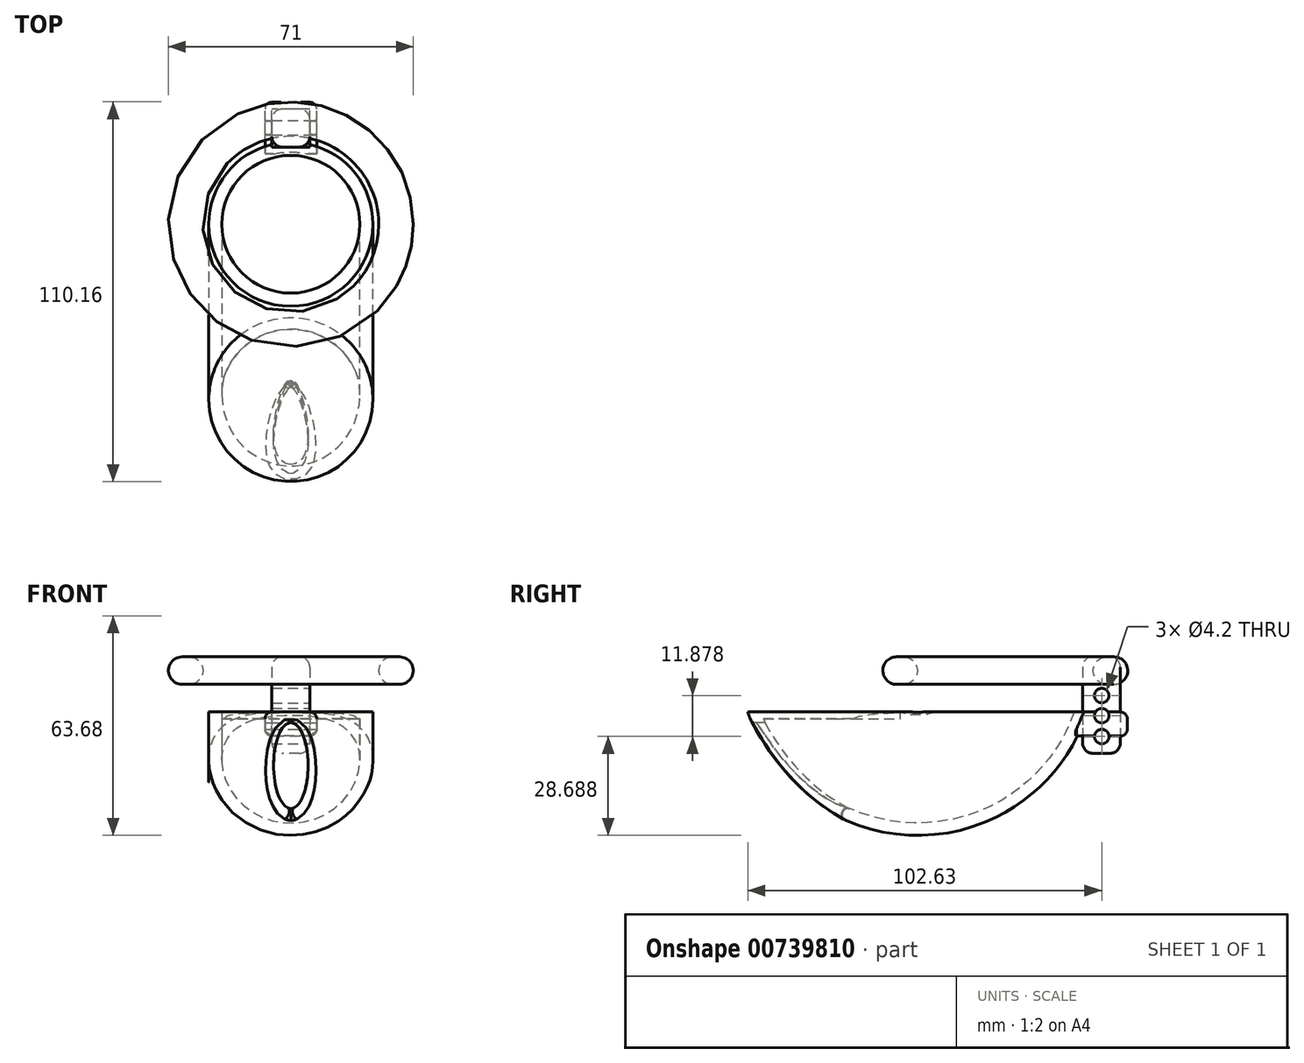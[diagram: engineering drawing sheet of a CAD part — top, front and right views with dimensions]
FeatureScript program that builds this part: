
annotation { "Feature Type Name" : "Feature", "Feature Type Description" : "" }
export const myFeature = defineFeature(function(context is Context, id is Id, definition is map)
    precondition{}
    {
        {
            var Q0;
            Q0=qCreatedBy(makeId("Front.planeOp"),FACE);
            cPlane(context, id + "F0", {"entities" : qUnion([Q0]), "cplaneType" : CPlaneType.OFFSET, "offset" : 25 * mm, "width" : 150 * mm, "height" : 150 * mm});
        }
        {
            var Q0;
            Q0=qCreatedBy(makeId("Top.planeOp"),FACE);
            var sketch = newSketch(context, id + "F1", { "sketchPlane" : qUnion([Q0])});
            skCircle(sketch, "E0", {"center": v(0, 0) * mm, "radius": 23.8 * mm});
            skCircle(sketch, "E1", {"center": v(0, 0) * mm, "radius": 20 * mm});
            skSolve(sketch);
        }
        {
            var Q0;
            Q0=qCreatedBy(makeId("Right.planeOp"),FACE);
            var sketch = newSketch(context, id + "F2", { "sketchPlane" : qUnion([Q0])});
            skArc(sketch, "E2", {"start": v(-55.13, 20.16) * mm, "mid": v(-35.74, -12.26) * mm, "end": v(0, 0) * mm});
            skSolve(sketch);
        }
        {
            var Q0;
            Q0=makeQuery(id+"F1.imprint","IMPRINT",FACE,{"disambiguationData":[TD([[makeQuery(id+"F1.imprint","IMPRINT",EDGE,{"derivedFrom":sQuery(id+"F1.wireOp",EDGE,"E0")}),1.0]])]});
            var Q1;
            Q1=sQuery(id+"F2.wireOp",EDGE,"E2");
            sweep(context, id + "F3", {"profiles" : qUnion([Q0]), "path" : qUnion([Q1])});
        }
        {
            var Q0;
            Q0=qCreatedBy(makeId("Right.planeOp"),FACE);
            var sketch = newSketch(context, id + "F4", { "sketchPlane" : qUnion([Q0])});
            skLineSegment(sketch, "E3.bottom", {"start": v(-24.7, 0) * mm, "end": v(-163.66, 0) * mm});
            skLineSegment(sketch, "E3.top", {"start": v(-24.7, 86.96) * mm, "end": v(-163.66, 86.96) * mm});
            skLineSegment(sketch, "E3.left", {"start": v(-24.7, 0) * mm, "end": v(-24.7, 86.96) * mm});
            skLineSegment(sketch, "E3.right", {"start": v(-163.66, 0) * mm, "end": v(-163.66, 86.96) * mm});
            skPoint(sketch, "E3.middle", {"position": v(-94.18, 43.48) * mm});
            skSolve(sketch);
        }
        {
            var Q0;
            Q0=qSketchRegion(id+"F4",true);
            extrude(context, id + "F5", {"entities" : qUnion([Q0]), "operationType" : NewBodyOperationType.REMOVE, "depth" : 25 * mm, "offsetDistance" : 25 * mm, "hasSecondDirection" : true, "secondDirectionOppositeDirection" : true, "secondDirectionDepth" : 25 * mm});
        }
        {
            var Q0;
            Q0=qCreatedBy(makeId("Top.planeOp"),FACE);
            var sketch = newSketch(context, id + "F6", { "sketchPlane" : qUnion([Q0])});
            skCircle(sketch, "E4", {"center": v(0, -50.93) * mm, "radius": 20.5 * mm});
            skSolve(sketch);
        }
        {
            var Q0;
            Q0=makeQuery(id+"F6.imprint","IMPRINT",FACE,{"disambiguationData":[TD([[makeQuery(id+"F6.imprint","IMPRINT",EDGE,{"derivedFrom":sQuery(id+"F6.wireOp",EDGE,"c734bf54-2df6-41e3-86b9-9994cdd1f29b")}),1.0]])]});
            var Q1;
            Q1=makeQuery(id+"F6.imprint","IMPRINT",FACE,{"disambiguationData":[TD([[makeQuery(id+"F6.imprint","IMPRINT",EDGE,{"derivedFrom":sQuery(id+"F6.wireOp",EDGE,"E4")}),1.0]])]});
            extrude(context, id + "F7", {"entities" : qUnion([Q0, Q1]), "operationType" : NewBodyOperationType.ADD, "oppositeDirection" : true, "depth" : 2 * mm, "offsetDistance" : 25 * mm});
        }
        {
            var Q0;
            Q0=qCreatedBy(id+"F0.planeOp",FACE);
            var sketch = newSketch(context, id + "F8", { "sketchPlane" : qUnion([Q0])});
            skEllipse(sketch, "E5", {"center": v(0, -15.52) * mm, "majorRadius": 12.5 * mm, "minorRadius": 5 * mm, "majorAxis": v(0, 1)});
            skSolve(sketch);
        }
        {
            var Q0;
            Q0=qSketchRegion(id+"F8",true);
            extrude(context, id + "F9", {"entities" : qUnion([Q0]), "operationType" : NewBodyOperationType.REMOVE, "depth" : 75 * mm, "offsetDistance" : 25 * mm, "hasSecondDirection" : true, "secondDirectionOppositeDirection" : false, "secondDirectionDepth" : 9.6 * mm});
        }
        {
            var Q0;
            Q0=makeQuery(id+"F9.boolean.opBoolean","INTERSECT",EDGE,{"derivedFrom":[makeQuery(id+"F3.opSweep","SWEPT_FACE",FACE,{"disambiguationData":[OSD([sQuery(id+"F1.wireOp",EDGE,"E0"),sQuery(id+"F2.wireOp",EDGE,"E2")])]}),makeQuery(id+"F9.opExtrude","SWEPT_FACE",FACE,{"disambiguationData":[OSD([sQuery(id+"F8.wireOp",EDGE,"E5")])]})]});
            fillet(context, id + "F10", {"entities" : qUnion([Q0]), "radius" : 1.8 * mm, "tangentPropagation" : true, "allowEdgeOverflow" : false});
        }
        {
            var Q0;
            Q0=qCreatedBy(makeId("Top.planeOp"),FACE);
            var sketch = newSketch(context, id + "F11", { "sketchPlane" : qUnion([Q0])});
            skLineSegment(sketch, "E6.bottom", {"start": v(7.5, 20.39) * mm, "end": v(-7.5, 20.39) * mm});
            skLineSegment(sketch, "E6.top", {"start": v(7.5, 35.39) * mm, "end": v(-7.5, 35.39) * mm});
            skLineSegment(sketch, "E6.left", {"start": v(7.5, 20.39) * mm, "end": v(7.5, 35.39) * mm});
            skLineSegment(sketch, "E6.right", {"start": v(-7.5, 20.39) * mm, "end": v(-7.5, 35.39) * mm});
            skPoint(sketch, "E6.middle", {"position": v(0, 27.89) * mm});
            skLineSegment(sketch, "E7.0", {"start": v(5.5, 33.39) * mm, "end": v(-5.5, 33.39) * mm});
            skLineSegment(sketch, "E7.1", {"start": v(5.5, 22.39) * mm, "end": v(5.5, 33.39) * mm});
            skLineSegment(sketch, "E7.2", {"start": v(5.5, 22.39) * mm, "end": v(-5.5, 22.39) * mm});
            skLineSegment(sketch, "E7.3", {"start": v(-5.5, 22.39) * mm, "end": v(-5.5, 33.39) * mm});
            skSolve(sketch);
        }
        {
            var Q0;
            Q0=makeQuery(id+"F11.imprint","IMPRINT",FACE,{"disambiguationData":[TD([[makeQuery(id+"F11.imprint","IMPRINT",EDGE,{"derivedFrom":sQuery(id+"F11.wireOp",EDGE,"E6.bottom")}),-1.0]])]});
            extrude(context, id + "F12", {"entities" : qUnion([Q0]), "operationType" : NewBodyOperationType.ADD, "oppositeDirection" : true, "depth" : 7 * mm, "offsetDistance" : 25 * mm});
        }
        {
            var Q0;
            Q0=makeQuery(id+"F11.imprint","IMPRINT",FACE,{"disambiguationData":[TD([[makeQuery(id+"F11.imprint","IMPRINT",EDGE,{"derivedFrom":sQuery(id+"F11.wireOp",EDGE,"E7.0")}),1.0]])]});
            extrude(context, id + "F13", {"entities" : qUnion([Q0]), "operationType" : NewBodyOperationType.REMOVE, "oppositeDirection" : true, "depth" : 5 * mm, "offsetDistance" : 25 * mm, "hasSecondDirection" : true, "secondDirectionOppositeDirection" : false, "secondDirectionDepth" : 5 * mm});
        }
        {
            var Q0;
            Q0=makeQuery(id+"F12.opExtrude","SWEPT_FACE",FACE,{"disambiguationData":[OSD([sQuery(id+"F11.wireOp",EDGE,"E6.top")])]});
            var Q1;
            Q1=makeQuery(id+"F12.opExtrude","CAP_EDGE",EDGE,{"disambiguationData":[OSD([sQuery(id+"F11.wireOp",EDGE,"E6.left")])],"isStart":false});
            var Q2;
            Q2=makeQuery(id+"F12.opExtrude","CAP_EDGE",EDGE,{"disambiguationData":[OSD([sQuery(id+"F11.wireOp",EDGE,"E6.left")])],"isStart":true});
            var Q3;
            Q3=makeQuery(id+"F12.opExtrude","CAP_EDGE",EDGE,{"disambiguationData":[OSD([sQuery(id+"F11.wireOp",EDGE,"E6.right")])],"isStart":true});
            var Q4;
            Q4=makeQuery(id+"F12.opExtrude","CAP_EDGE",EDGE,{"disambiguationData":[OSD([sQuery(id+"F11.wireOp",EDGE,"E6.right")])],"isStart":false});
            fillet(context, id + "F14", {"entities" : qUnion([Q0, Q1, Q2, Q3, Q4]), "radius" : 2 * mm, "tangentPropagation" : true, "allowEdgeOverflow" : false});
        }
        {
            var Q0;
            Q0=qCreatedBy(makeId("Top.planeOp"),FACE);
            var sketch = newSketch(context, id + "F15", { "sketchPlane" : qUnion([Q0])});
            skCircle(sketch, "E8", {"center": v(0, 0) * mm, "radius": 25.5 * mm});
            skCircle(sketch, "E9.0", {"center": v(0, 0) * mm, "radius": 35.5 * mm});
            skSolve(sketch);
        }
        {
            var Q0;
            Q0 = qSketchRegion(id + "F15", true);
            extrude(context, id + "F16", {"entities" : qUnion([Q0]), "depth" : 16 * mm, "offsetDistance" : 25 * mm, "hasSecondDirection" : true, "secondDirectionOppositeDirection" : false, "secondDirectionDepth" : 8 * mm});
        }
        {
            var Q0;
            Q0=makeQuery(id+"F16.opExtrude","SWEPT_FACE",FACE,{"disambiguationData":[OSD([sQuery(id+"F15.wireOp",EDGE,"E9.0")])]});
            var Q1;
            Q1=makeQuery(id+"F16.opExtrude","SWEPT_FACE",FACE,{"disambiguationData":[OSD([sQuery(id+"F15.wireOp",EDGE,"E8")])]});
            fillet(context, id + "F17", {"entities" : qUnion([Q0, Q1]), "radius" : 4 * mm, "tangentPropagation" : true, "allowEdgeOverflow" : false});
        }
        {
            var Q0;
            Q0=makeQuery(id+"F11.imprint","IMPRINT",FACE,{"disambiguationData":[TD([[makeQuery(id+"F11.imprint","IMPRINT",EDGE,{"derivedFrom":sQuery(id+"F11.wireOp",EDGE,"E7.0")}),1.0]])]});
            extrude(context, id + "F18", {"entities" : qUnion([Q0]), "depth" : 16 * mm, "offsetDistance" : 25 * mm, "hasSecondDirection" : true, "secondDirectionOppositeDirection" : true, "secondDirectionDepth" : 12 * mm});
        }
        {
            var Q0;
            Q0=makeQuery(id+"FuZBCL0iS8PPMPQ_3.boolean.opBoolean","COPY",FACE,{"derivedFrom":makeQuery(id+"FuZBCL0iS8PPMPQ_3.opThicken","CAP_FACE",FACE,{"disambiguationData":[OSD([sQuery(id+"F11.wireOp",EDGE,"E7.0")])],"isStart":false})});
            var Q1;
            Q1=makeQuery(id+"FuZBCL0iS8PPMPQ_3.boolean.opBoolean","COPY",FACE,{"derivedFrom":makeQuery(id+"FuZBCL0iS8PPMPQ_3.opThicken","CAP_FACE",FACE,{"disambiguationData":[OSD([sQuery(id+"F11.wireOp",EDGE,"E7.2")])],"isStart":false})});
            var Q2;
            Q2=makeQuery(id+"F18.opExtrude","SWEPT_EDGE",EDGE,{"disambiguationData":[OSD([sQuery(id+"F11.wireOp",EDGE,"E7.0"),sQuery(id+"F11.wireOp",EDGE,"E7.1")])]});
            var Q3;
            Q3=makeQuery(id+"F18.opExtrude","SWEPT_EDGE",EDGE,{"disambiguationData":[OSD([sQuery(id+"F11.wireOp",EDGE,"E7.1"),sQuery(id+"F11.wireOp",EDGE,"E7.2")])]});
            var Q4;
            Q4=makeQuery(id+"F18.opExtrude","SWEPT_EDGE",EDGE,{"disambiguationData":[OSD([sQuery(id+"F11.wireOp",EDGE,"E7.0"),sQuery(id+"F11.wireOp",EDGE,"E7.3")])]});
            var Q5;
            Q5=makeQuery(id+"F18.opExtrude","SWEPT_EDGE",EDGE,{"disambiguationData":[OSD([sQuery(id+"F11.wireOp",EDGE,"E7.2"),sQuery(id+"F11.wireOp",EDGE,"E7.3")])]});
            var Q6;
            Q6=makeQuery(id+"F18.opExtrude","CAP_FACE",FACE,{"disambiguationData":[OSD([sQuery(id+"F11.wireOp",EDGE,"E7.0"),sQuery(id+"F11.wireOp",EDGE,"E7.1"),sQuery(id+"F11.wireOp",EDGE,"E7.2"),sQuery(id+"F11.wireOp",EDGE,"E7.3")])],"isStart":true});
            var Q7;
            Q7=makeQuery(id+"F18.opExtrude","CAP_FACE",FACE,{"disambiguationData":[OSD([sQuery(id+"F11.wireOp",EDGE,"E7.0"),sQuery(id+"F11.wireOp",EDGE,"E7.1"),sQuery(id+"F11.wireOp",EDGE,"E7.2"),sQuery(id+"F11.wireOp",EDGE,"E7.3")])],"isStart":false});
            fillet(context, id + "F19", {"entities" : qUnion([Q0, Q1, Q2, Q3, Q4, Q5, Q6, Q7]), "radius" : 3 * mm, "tangentPropagation" : true, "allowEdgeOverflow" : false});
        }
        {
            var Q0;
            Q0=qCreatedBy(makeId("Right.planeOp"),FACE);
            var sketch = newSketch(context, id + "F20", { "sketchPlane" : qUnion([Q0])});
            skCircle(sketch, "E10", {"center": v(27.97, -7.13) * mm, "radius": 2.1 * mm});
            skPoint(sketch, "E10.centerSnap0", {"position": v(27.97, -9) * mm});
            skCircle(sketch, "E11", {"center": v(27.97, -1.09) * mm, "radius": 2.1 * mm});
            skCircle(sketch, "E12", {"center": v(27.97, 4.75) * mm, "radius": 2.1 * mm});
            skSolve(sketch);
        }
        {
            var Q0;
            Q0 = qSketchRegion(id + "F20", true);
            extrude(context, id + "F21", {"entities" : qUnion([Q0]), "operationType" : NewBodyOperationType.REMOVE, "oppositeDirection" : true, "depth" : 25 * mm, "offsetDistance" : 25 * mm, "hasSecondDirection" : true, "secondDirectionOppositeDirection" : false, "secondDirectionDepth" : 25 * mm});
        }
    });
